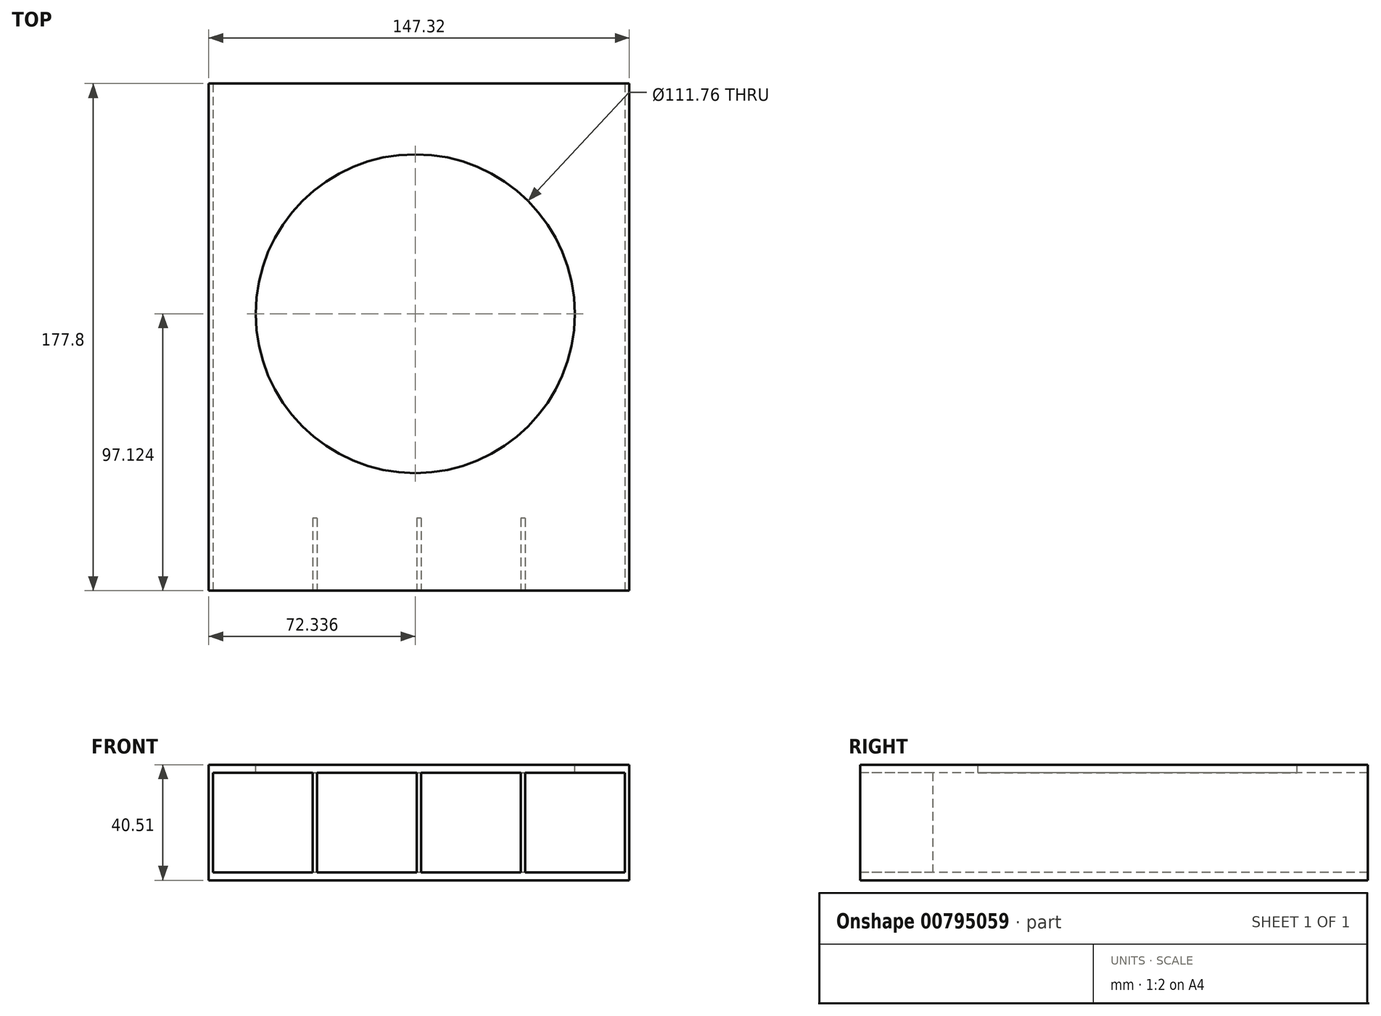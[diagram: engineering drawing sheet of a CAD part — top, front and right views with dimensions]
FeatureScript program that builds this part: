
annotation { "Feature Type Name" : "Feature", "Feature Type Description" : "" }
export const myFeature = defineFeature(function(context is Context, id is Id, definition is map)
    precondition{}
    {
        {
            var Q0;
            Q0=qCreatedBy(makeId("Front.planeOp"),FACE);
            var sketch = newSketch(context, id + "F0", { "sketchPlane" : qUnion([Q0])});
            skLineSegment(sketch, "E0.bottom", {"start": v(-50.77, 35.5) * mm, "end": v(96.55, 35.5) * mm});
            skLineSegment(sketch, "E1", {"start": v(96.55, 35.5) * mm, "end": v(96.55, -5.01) * mm});
            skLineSegment(sketch, "E2.bottom", {"start": v(-14.32, 32.7) * mm, "end": v(-49.25, 32.7) * mm});
            skLineSegment(sketch, "E2.top", {"start": v(-14.32, -2.22) * mm, "end": v(-49.25, -2.22) * mm});
            skLineSegment(sketch, "E2.left", {"start": v(-14.32, 32.7) * mm, "end": v(-14.32, -2.22) * mm});
            skLineSegment(sketch, "E2.right", {"start": v(-49.25, 32.7) * mm, "end": v(-49.25, -2.22) * mm});
            skLineSegment(sketch, "E3.bottom", {"start": v(22.13, 32.7) * mm, "end": v(-12.8, 32.7) * mm});
            skLineSegment(sketch, "E3.top", {"start": v(22.13, -2.22) * mm, "end": v(-12.8, -2.22) * mm});
            skLineSegment(sketch, "E3.left", {"start": v(22.13, 32.7) * mm, "end": v(22.13, -2.22) * mm});
            skLineSegment(sketch, "E3.right", {"start": v(-12.8, 32.7) * mm, "end": v(-12.8, -2.22) * mm});
            skLineSegment(sketch, "E4.bottom", {"start": v(58.58, 32.7) * mm, "end": v(23.65, 32.7) * mm});
            skLineSegment(sketch, "E4.top", {"start": v(58.58, -2.22) * mm, "end": v(23.65, -2.22) * mm});
            skLineSegment(sketch, "E4.left", {"start": v(58.58, 32.7) * mm, "end": v(58.58, -2.22) * mm});
            skLineSegment(sketch, "E4.right", {"start": v(23.65, 32.7) * mm, "end": v(23.65, -2.22) * mm});
            skLineSegment(sketch, "E5.bottom", {"start": v(95.03, 32.7) * mm, "end": v(60.1, 32.7) * mm});
            skLineSegment(sketch, "E5.top", {"start": v(95.03, -2.22) * mm, "end": v(60.1, -2.22) * mm});
            skLineSegment(sketch, "E5.left", {"start": v(95.03, 32.7) * mm, "end": v(95.03, -2.22) * mm});
            skLineSegment(sketch, "E5.right", {"start": v(60.1, 32.7) * mm, "end": v(60.1, -2.22) * mm});
            skLineSegment(sketch, "E6", {"start": v(95.03, -2.22) * mm, "end": v(-49.25, -2.22) * mm});
            skLineSegment(sketch, "E7", {"start": v(95.03, 32.7) * mm, "end": v(-49.25, 32.7) * mm});
            skLineSegment(sketch, "E8", {"start": v(-50.77, 35.5) * mm, "end": v(-50.77, -5.01) * mm});
            skLineSegment(sketch, "E9", {"start": v(96.55, -5.01) * mm, "end": v(-50.77, -5.01) * mm});
            skSolve(sketch);
        }
        {
            var Q0;
            Q0=makeQuery(id+"F0.imprint","IMPRINT",FACE,{"disambiguationData":[TD([[makeQuery(id+"F0.imprint","IMPRINT",EDGE,{"derivedFrom":sQuery(id+"F0.wireOp",EDGE,"E0.bottom")}),-1.0]])]});
            var Q1;
            {var subQ0=sQuery(id+"F0.wireOp",EDGE,"E2.left");Q1=makeQuery(id+"F0.imprint","IMPRINT",FACE,{"disambiguationData":[TD([[makeQuery(id+"F0.imprint","IMPRINT",EDGE,{"derivedFrom":subQ0}),1.0]])]});}
            var Q2;
            {var subQ0=sQuery(id+"F0.wireOp",EDGE,"E3.left");Q2=makeQuery(id+"F0.imprint","IMPRINT",FACE,{"disambiguationData":[TD([[makeQuery(id+"F0.imprint","IMPRINT",EDGE,{"derivedFrom":subQ0}),1.0]])]});}
            var Q3;
            {var subQ0=sQuery(id+"F0.wireOp",EDGE,"E4.left");Q3=makeQuery(id+"F0.imprint","IMPRINT",FACE,{"disambiguationData":[TD([[makeQuery(id+"F0.imprint","IMPRINT",EDGE,{"derivedFrom":subQ0}),1.0]])]});}
            var Q4;
            {var subQ5=sQuery(id+"F0.wireOp",EDGE,"E5.left");Q4=makeQuery(id+"F0.imprint","IMPRINT",FACE,{"disambiguationData":[TD([[makeQuery(id+"F0.imprint","IMPRINT",EDGE,{"derivedFrom":subQ5}),1.0]])]});}
            var Q5;
            {var subQ8=sQuery(id+"F0.wireOp",EDGE,"E9");Q5=makeQuery(id+"F0.imprint","IMPRINT",FACE,{"disambiguationData":[TD([[makeQuery(id+"F0.imprint","IMPRINT",EDGE,{"derivedFrom":subQ8}),-1.0]])]});}
            var Q6;
            {var subQ0=sQuery(id+"F0.wireOp",EDGE,"E2.right");Q6=makeQuery(id+"F0.imprint","IMPRINT",FACE,{"disambiguationData":[TD([[makeQuery(id+"F0.imprint","IMPRINT",EDGE,{"derivedFrom":subQ0}),-1.0]])]});}
            extrude(context, id + "F1", {"entities" : qUnion([Q0, Q1, Q2, Q3, Q4, Q5, Q6]), "oppositeDirection" : true, "depth" : 25.4 * mm, "offsetDistance" : 25.4 * mm});
        }
        {
            var Q0;
            Q0=makeQuery(id+"F1.opExtrude","CAP_FACE",FACE,{"disambiguationData":[OSD([sQuery(id+"F0.wireOp",EDGE,"E0.bottom"),sQuery(id+"F0.wireOp",EDGE,"E1"),sQuery(id+"F0.wireOp",EDGE,"E2.left"),sQuery(id+"F0.wireOp",EDGE,"E2.right"),sQuery(id+"F0.wireOp",EDGE,"E3.left"),sQuery(id+"F0.wireOp",EDGE,"E3.right"),sQuery(id+"F0.wireOp",EDGE,"E4.left"),sQuery(id+"F0.wireOp",EDGE,"E4.right"),sQuery(id+"F0.wireOp",EDGE,"E5.left"),sQuery(id+"F0.wireOp",EDGE,"E5.right"),sQuery(id+"F0.wireOp",EDGE,"E6"),sQuery(id+"F0.wireOp",EDGE,"E7"),sQuery(id+"F0.wireOp",EDGE,"E8"),sQuery(id+"F0.wireOp",EDGE,"E9")])],"isStart":false});
            var sketch = newSketch(context, id + "F2", { "sketchPlane" : qUnion([Q0])});
            skLineSegment(sketch, "E10", {"start": v(-95.03, 32.7) * mm, "end": v(-96.55, 32.7) * mm});
            skLineSegment(sketch, "E11", {"start": v(-96.55, 32.7) * mm, "end": v(50.77, 32.7) * mm});
            skLineSegment(sketch, "E12", {"start": v(49.25, -2.22) * mm, "end": v(50.77, -2.22) * mm});
            skLineSegment(sketch, "E13", {"start": v(50.77, -2.22) * mm, "end": v(-96.55, -2.22) * mm});
            skSolve(sketch);
        }
        {
            var Q0;
            {var subQ1=makeQuery(id+"F1.opExtrude","CAP_EDGE",EDGE,{"disambiguationData":[OSD([sQuery(id+"F0.wireOp",EDGE,"E5.left")])],"isStart":false});Q0=makeQuery(id+"F2.imprint","IMPRINT",FACE,{"disambiguationData":[TD([[makeQuery(id+"F2.imprint","IMPRINT",EDGE,{"derivedFrom":subQ1}),-1.0]])]});}
            var Q1;
            {var subQ4=makeQuery(id+"F1.opExtrude","CAP_EDGE",EDGE,{"disambiguationData":[OSD([sQuery(id+"F0.wireOp",EDGE,"E9")])],"isStart":false});Q1=makeQuery(id+"F2.imprint","IMPRINT",FACE,{"disambiguationData":[TD([[makeQuery(id+"F2.imprint","IMPRINT",EDGE,{"derivedFrom":subQ4}),1.0]])]});}
            var Q2;
            {var subQ4=makeQuery(id+"F1.opExtrude","CAP_EDGE",EDGE,{"disambiguationData":[OSD([sQuery(id+"F0.wireOp",EDGE,"E0.bottom")])],"isStart":false});Q2=makeQuery(id+"F2.imprint","IMPRINT",FACE,{"disambiguationData":[TD([[makeQuery(id+"F2.imprint","IMPRINT",EDGE,{"derivedFrom":subQ4}),1.0]])]});}
            var Q3;
            {var subQ1=makeQuery(id+"F1.opExtrude","CAP_EDGE",EDGE,{"disambiguationData":[OSD([sQuery(id+"F0.wireOp",EDGE,"E2.right")])],"isStart":false});Q3=makeQuery(id+"F2.imprint","IMPRINT",FACE,{"disambiguationData":[TD([[makeQuery(id+"F2.imprint","IMPRINT",EDGE,{"derivedFrom":subQ1}),1.0]])]});}
            extrude(context, id + "F3", {"entities" : qUnion([Q0, Q1, Q2, Q3]), "operationType" : NewBodyOperationType.ADD, "depth" : 152.4 * mm, "offsetDistance" : 25.4 * mm});
        }
        {
            var Q0;
            {var subQ0=sQuery(id+"F0.wireOp",EDGE,"E0.bottom");Q0=makeQuery(id+"F3.boolean.opBoolean","MERGE",FACE,{"derivedFrom":[makeQuery(id+"F1.opExtrude","SWEPT_FACE",FACE,{"disambiguationData":[OSD([subQ0])]}),makeQuery(id+"F3.opExtrude","SWEPT_FACE",FACE,{"disambiguationData":[OSD([subQ0])]})]});}
            var sketch = newSketch(context, id + "F4", { "sketchPlane" : qUnion([Q0])});
            skCircle(sketch, "E14", {"center": v(21.57, 97.12) * mm, "radius": 55.88 * mm});
            skSolve(sketch);
        }
        {
            var Q0;
            Q0=makeQuery(id+"F4.imprint","IMPRINT",FACE,{"disambiguationData":[TD([[makeQuery(id+"F4.imprint","IMPRINT",EDGE,{"derivedFrom":sQuery(id+"F4.wireOp",EDGE,"E14")}),1.0]])]});
            extrude(context, id + "F5", {"entities" : qUnion([Q0]), "operationType" : NewBodyOperationType.REMOVE, "oppositeDirection" : true, "depth" : 25.4 * mm, "offsetDistance" : 25.4 * mm});
        }
    });
